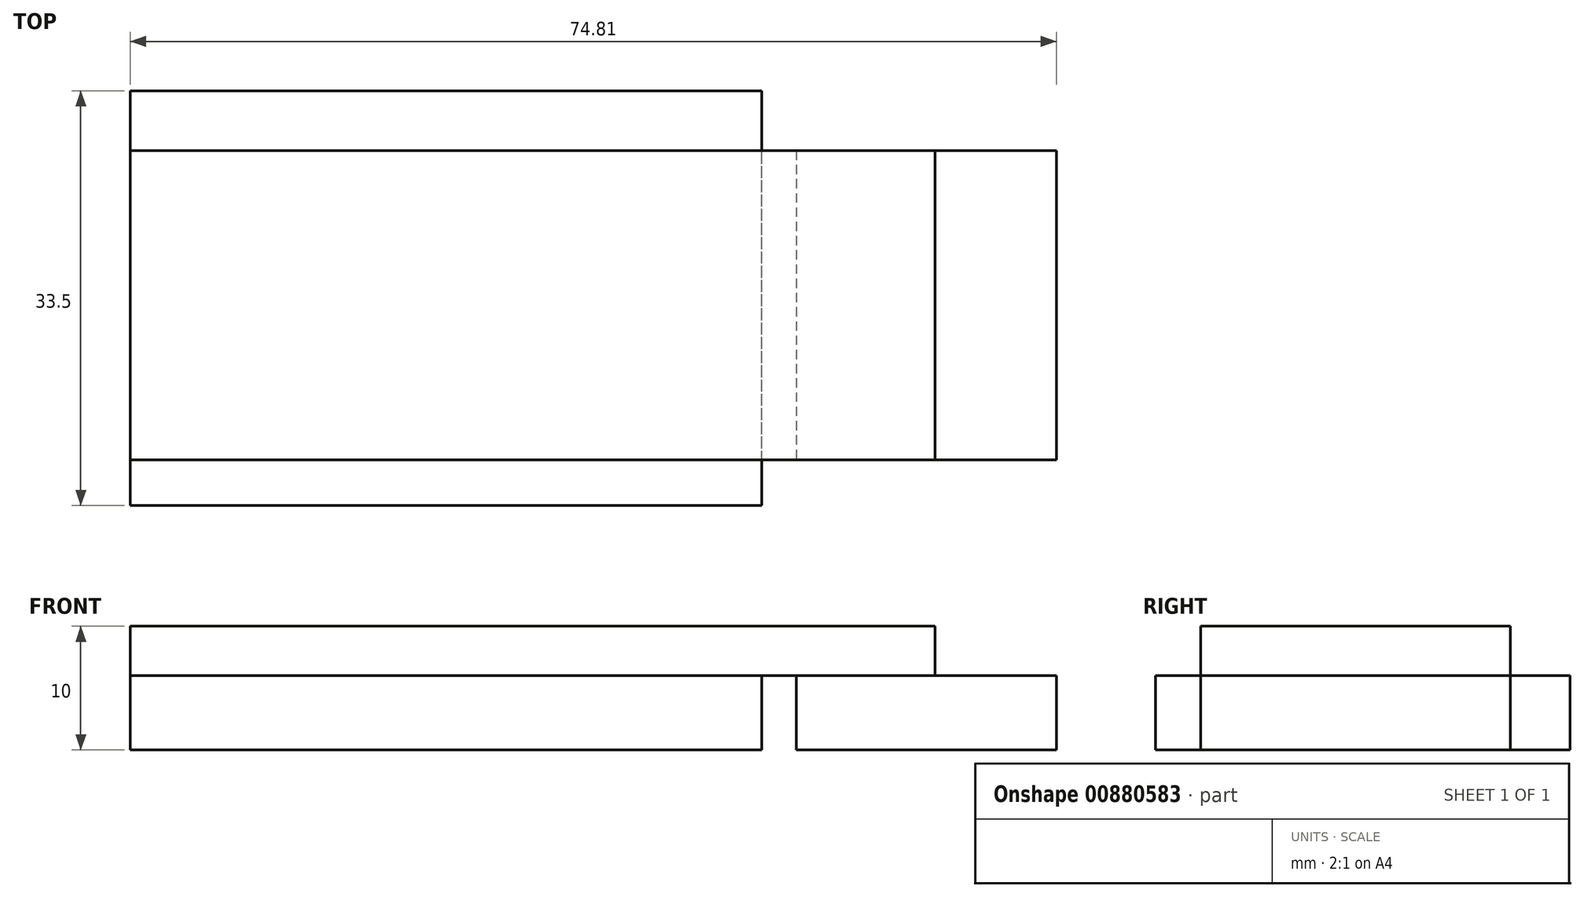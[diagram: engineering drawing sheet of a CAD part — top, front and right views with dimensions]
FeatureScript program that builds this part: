
annotation { "Feature Type Name" : "Feature", "Feature Type Description" : "" }
export const myFeature = defineFeature(function(context is Context, id is Id, definition is map)
    precondition{}
    {
        {
            var Q0;
            Q0=qCreatedBy(makeId("Top.planeOp"),FACE);
            var sketch = newSketch(context, id + "F0", { "sketchPlane" : qUnion([Q0])});
            skLineSegment(sketch, "E0.bottom", {"start": v(0, 0) * mm, "end": v(51, 0) * mm});
            skLineSegment(sketch, "E0.top", {"start": v(0, 33.5) * mm, "end": v(51, 33.5) * mm});
            skLineSegment(sketch, "E0.left", {"start": v(0, 0) * mm, "end": v(0, 33.5) * mm});
            skLineSegment(sketch, "E0.right", {"start": v(51, 0) * mm, "end": v(51, 33.5) * mm});
            skSolve(sketch);
        }
        {
            var Q0;
            Q0=makeQuery(id+"F0.imprint","IMPRINT",FACE,{"disambiguationData":[TD([[makeQuery(id+"F0.imprint","IMPRINT",EDGE,{"derivedFrom":sQuery(id+"F0.wireOp",EDGE,"E0.bottom")}),1.0]])]});
            extrude(context, id + "F1", {"entities" : qUnion([Q0]), "depth" : 6 * mm, "offsetDistance" : 25.4 * mm});
        }
        {
            var Q0;
            Q0=makeQuery(id+"F1.opExtrude","CAP_FACE",FACE,{"disambiguationData":[OSD([sQuery(id+"F0.wireOp",EDGE,"E0.bottom"),sQuery(id+"F0.wireOp",EDGE,"E0.top"),sQuery(id+"F0.wireOp",EDGE,"E0.left"),sQuery(id+"F0.wireOp",EDGE,"E0.right")])],"isStart":false});
            var sketch = newSketch(context, id + "F2", { "sketchPlane" : qUnion([Q0])});
            skLineSegment(sketch, "E1.bottom", {"start": v(0, 3.68) * mm, "end": v(65, 3.68) * mm});
            skLineSegment(sketch, "E1.top", {"start": v(0, 28.68) * mm, "end": v(65, 28.68) * mm});
            skLineSegment(sketch, "E1.left", {"start": v(0, 3.68) * mm, "end": v(0, 28.68) * mm});
            skLineSegment(sketch, "E1.right", {"start": v(65, 3.68) * mm, "end": v(65, 28.68) * mm});
            skSolve(sketch);
        }
        {
            var Q0;
            Q0 = qSketchRegion(id + "F2", true);
            var Q1;
            Q1 = qSketchRegion(id + "F4", true);
            extrude(context, id + "F3", {"entities" : qUnion([Q0, Q1]), "depth" : 4 * mm, "offsetDistance" : 25.4 * mm});
        }
        {
            var Q0;
            Q0=makeQuery(id+"F3.opExtrude","CAP_FACE",FACE,{"disambiguationData":[OSD([sQuery(id+"F2.wireOp",EDGE,"E1.bottom"),sQuery(id+"F2.wireOp",EDGE,"E1.top"),sQuery(id+"F2.wireOp",EDGE,"E1.left"),sQuery(id+"F2.wireOp",EDGE,"E1.right")])],"isStart":true});
            var sketch = newSketch(context, id + "F4", { "sketchPlane" : qUnion([Q0])});
            skLineSegment(sketch, "E2.bottom", {"start": v(53.81, -28.68) * mm, "end": v(74.81, -28.68) * mm});
            skLineSegment(sketch, "E2.top", {"start": v(53.81, -3.68) * mm, "end": v(74.81, -3.68) * mm});
            skLineSegment(sketch, "E2.left", {"start": v(53.81, -28.68) * mm, "end": v(53.81, -3.68) * mm});
            skLineSegment(sketch, "E2.right", {"start": v(74.81, -28.68) * mm, "end": v(74.81, -3.68) * mm});
            skLineSegment(sketch, "E3", {"start": v(65, -16.18) * mm, "end": v(74.81, -16.18) * mm, "construction": true});
            skSolve(sketch);
        }
        {
            var Q0;
            Q0 = qSketchRegion(id + "F4", true);
            extrude(context, id + "F5", {"entities" : qUnion([Q0]), "depth" : 6 * mm, "offsetDistance" : 25.4 * mm});
        }
    });
